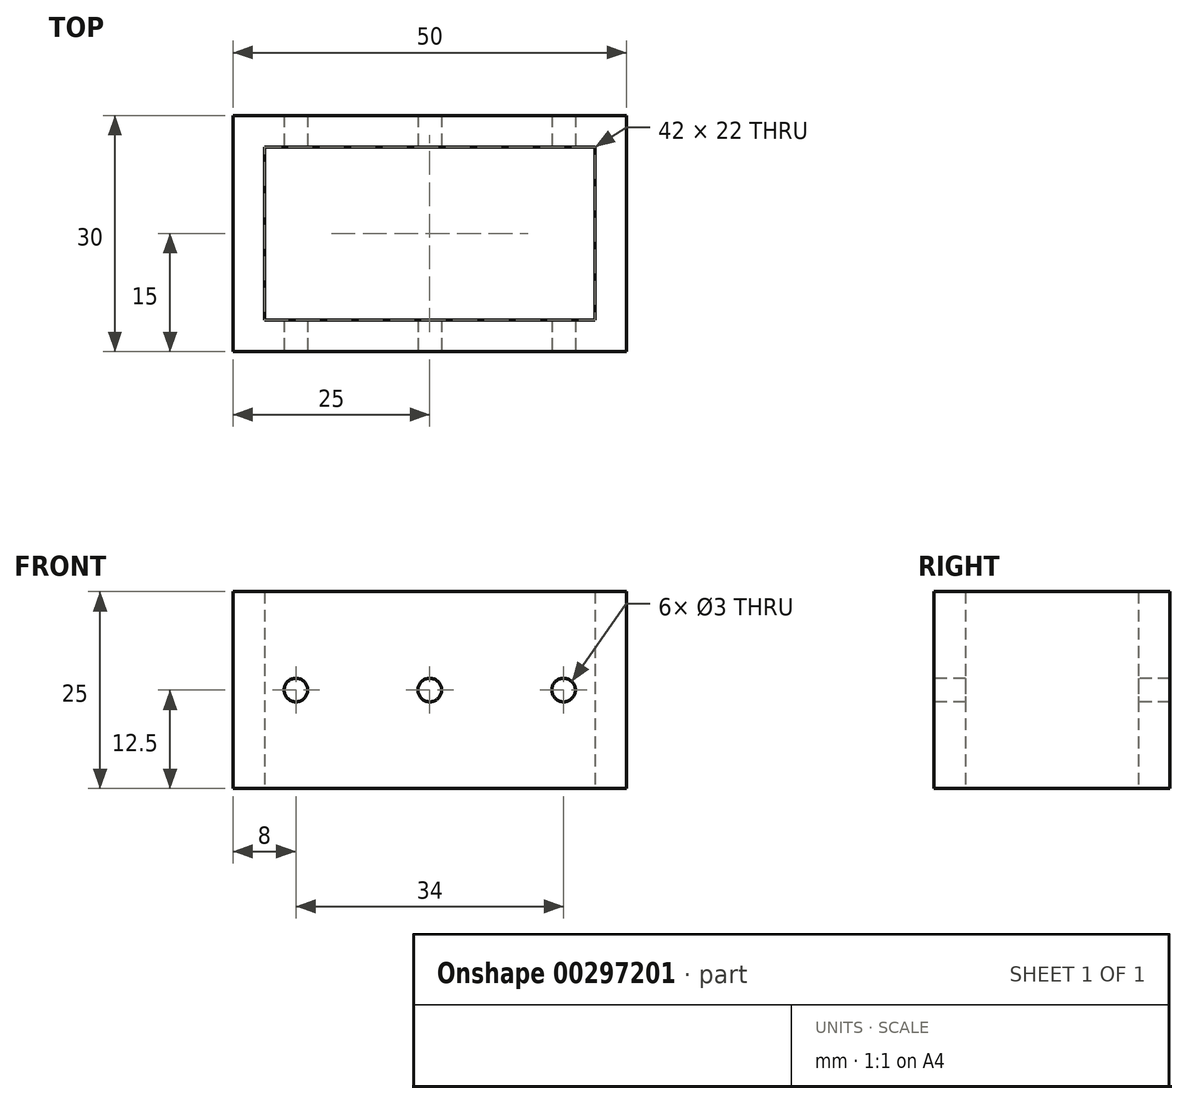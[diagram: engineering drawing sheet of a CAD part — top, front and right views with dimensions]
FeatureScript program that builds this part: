
annotation { "Feature Type Name" : "Feature", "Feature Type Description" : "" }
export const myFeature = defineFeature(function(context is Context, id is Id, definition is map)
    precondition{}
    {
        {
            var Q0;
            Q0=qCreatedBy(makeId("Top.planeOp"),FACE);
            var sketch = newSketch(context, id + "F0", { "sketchPlane" : qUnion([Q0])});
            skLineSegment(sketch, "E0.bottom", {"start": v(0, 0) * mm, "end": v(50, 0) * mm});
            skLineSegment(sketch, "E0.top", {"start": v(0, -30) * mm, "end": v(50, -30) * mm});
            skLineSegment(sketch, "E0.left", {"start": v(0, 0) * mm, "end": v(0, -30) * mm});
            skLineSegment(sketch, "E0.right", {"start": v(50, 0) * mm, "end": v(50, -30) * mm});
            skLineSegment(sketch, "E1.0", {"start": v(4, -4) * mm, "end": v(46, -4) * mm});
            skLineSegment(sketch, "E1.1", {"start": v(4, -4) * mm, "end": v(4, -26) * mm});
            skLineSegment(sketch, "E1.2", {"start": v(4, -26) * mm, "end": v(46, -26) * mm});
            skLineSegment(sketch, "E1.3", {"start": v(46, -4) * mm, "end": v(46, -26) * mm});
            skSolve(sketch);
        }
        {
            var Q0;
            Q0 = qSketchRegion(id + "F0", true);
            extrude(context, id + "F1", {"entities" : qUnion([Q0]), "depth" : 25 * mm});
        }
        {
            var Q0;
            Q0=makeQuery(id+"F1.opExtrude","SWEPT_FACE",FACE,{"disambiguationData":[OSD([sQuery(id+"F0.wireOp",EDGE,"E0.top")])]});
            var sketch = newSketch(context, id + "F2", { "sketchPlane" : qUnion([Q0])});
            skLineSegment(sketch, "E2", {"start": v(0, 12.5) * mm, "end": v(50, 12.5) * mm, "construction": true});
            skLineSegment(sketch, "E3", {"start": v(25, 0) * mm, "end": v(25, 25) * mm, "construction": true});
            skCircle(sketch, "E4", {"center": v(25, 12.5) * mm, "radius": 1.5 * mm});
            skLineSegment(sketch, "E5", {"start": v(42, 0) * mm, "end": v(42, 25) * mm, "construction": true});
            skLineSegment(sketch, "E6", {"start": v(8, 0) * mm, "end": v(8, 25) * mm, "construction": true});
            skCircle(sketch, "E7", {"center": v(8, 12.5) * mm, "radius": 1.5 * mm});
            skCircle(sketch, "E8", {"center": v(42, 12.5) * mm, "radius": 1.5 * mm});
            skSolve(sketch);
        }
        {
            var Q0;
            Q0 = qSketchRegion(id + "F2", true);
            extrude(context, id + "F3", {"entities" : qUnion([Q0]), "operationType" : NewBodyOperationType.REMOVE, "oppositeDirection" : true, "depth" : 35 * mm});
        }
    });
